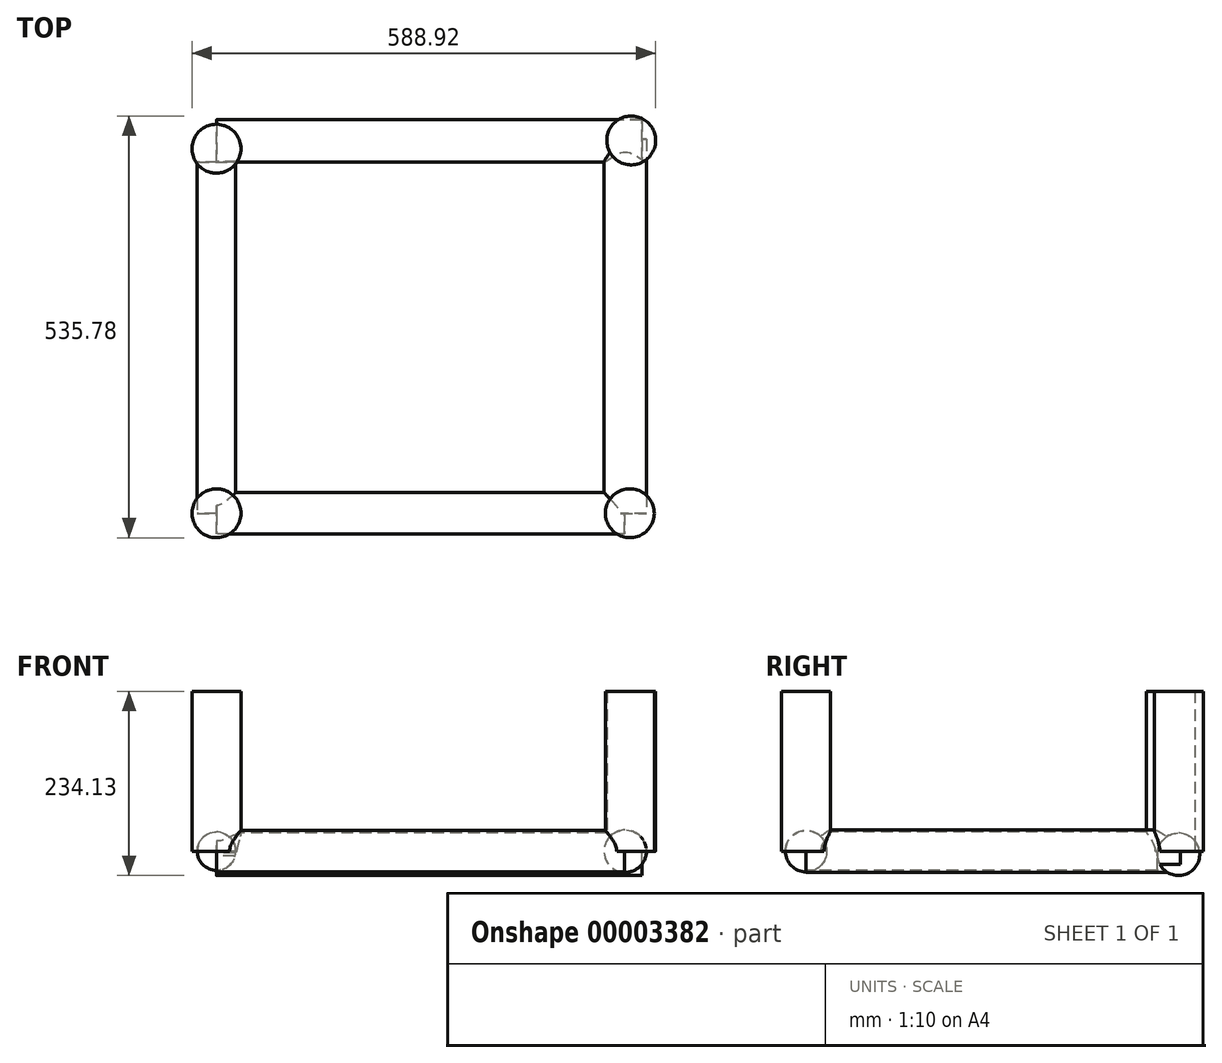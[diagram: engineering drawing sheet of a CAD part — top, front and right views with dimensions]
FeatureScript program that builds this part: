
annotation { "Feature Type Name" : "Feature", "Feature Type Description" : "" }
export const myFeature = defineFeature(function(context is Context, id is Id, definition is map)
    precondition{}
    {
        {
            var Q0;
            Q0=qCreatedBy(makeId("Front.planeOp"),FACE);
            var sketch = newSketch(context, id + "F0", { "sketchPlane" : qUnion([Q0])});
            skCircle(sketch, "E0", {"center": v(0, 0) * mm, "radius": 24.35 * mm});
            skSolve(sketch);
        }
        {
            var Q0;
            Q0=makeQuery(id+"F0.imprint","IMPRINT",FACE,{"disambiguationData":[TD([[makeQuery(id+"F0.imprint","IMPRINT",EDGE,{"derivedFrom":sQuery(id+"F0.wireOp",EDGE,"E0")}),1.0]])]});
            extrude(context, id + "F1", {"entities" : qUnion([Q0]), "oppositeDirection" : true, "depth" : 446.25 * mm});
        }
        {
            var Q0;
            Q0=qCreatedBy(makeId("Right.planeOp"),FACE);
            var sketch = newSketch(context, id + "F2", { "sketchPlane" : qUnion([Q0])});
            skCircle(sketch, "E1", {"center": v(0, 0) * mm, "radius": 26.23 * mm});
            skSolve(sketch);
        }
        {
            var Q0;
            Q0=makeQuery(id+"F2.imprint","IMPRINT",FACE,{"disambiguationData":[TD([[makeQuery(id+"F2.imprint","IMPRINT",EDGE,{"derivedFrom":sQuery(id+"F2.wireOp",EDGE,"E1")}),1.0]])]});
            extrude(context, id + "F3", {"entities" : qUnion([Q0]), "operationType" : NewBodyOperationType.ADD, "depth" : 518.32 * mm});
        }
        {
            var Q0;
            Q0=qCreatedBy(makeId("Front.planeOp"),FACE);
            var sketch = newSketch(context, id + "F4", { "sketchPlane" : qUnion([Q0])});
            skCircle(sketch, "E2", {"center": v(519.19, 0) * mm, "radius": 26.9 * mm});
            skSolve(sketch);
        }
        {
            var Q0;
            Q0=makeQuery(id+"F4.imprint","IMPRINT",FACE,{"disambiguationData":[TD([[makeQuery(id+"F4.imprint","IMPRINT",EDGE,{"derivedFrom":sQuery(id+"F4.wireOp",EDGE,"E2")}),1.0]])]});
            extrude(context, id + "F5", {"entities" : qUnion([Q0]), "operationType" : NewBodyOperationType.ADD, "oppositeDirection" : true, "depth" : 475.33 * mm});
        }
        {
            var Q0;
            Q0=qCreatedBy(makeId("Right.planeOp"),FACE);
            var sketch = newSketch(context, id + "F6", { "sketchPlane" : qUnion([Q0])});
            skCircle(sketch, "E3", {"center": v(473.13, -3.98) * mm, "radius": 26.95 * mm});
            skSolve(sketch);
        }
        {
            var Q0;
            Q0=makeQuery(id+"F6.imprint","IMPRINT",FACE,{"disambiguationData":[TD([[makeQuery(id+"F6.imprint","IMPRINT",EDGE,{"derivedFrom":sQuery(id+"F6.wireOp",EDGE,"E3")}),1.0]])]});
            extrude(context, id + "F7", {"entities" : qUnion([Q0]), "operationType" : NewBodyOperationType.ADD, "depth" : 540.38 * mm});
        }
        {
            var Q0;
            Q0=qCreatedBy(makeId("Top.planeOp"),FACE);
            var sketch = newSketch(context, id + "F8", { "sketchPlane" : qUnion([Q0])});
            skCircle(sketch, "E4", {"center": v(0, 0) * mm, "radius": 31.05 * mm});
            skCircle(sketch, "E5", {"center": v(0, 463.12) * mm, "radius": 31.05 * mm});
            skCircle(sketch, "E6", {"center": v(526.82, 473.68) * mm, "radius": 31.05 * mm});
            skCircle(sketch, "E7", {"center": v(525.12, 0) * mm, "radius": 31.05 * mm});
            skSolve(sketch);
        }
        {
            var Q0;
            {Q0=qUnion([makeQuery(id+"F8.imprint","IMPRINT",FACE,{"disambiguationData":[TD([[makeQuery(id+"F8.imprint","IMPRINT",EDGE,{"derivedFrom":sQuery(id+"F8.wireOp",EDGE,"E4")}),1.0]])]}),makeQuery(id+"F8.imprint","IMPRINT",FACE,{"disambiguationData":[TD([[makeQuery(id+"F8.imprint","IMPRINT",EDGE,{"derivedFrom":sQuery(id+"F8.wireOp",EDGE,"E5")}),1.0]])]}),makeQuery(id+"F8.imprint","IMPRINT",FACE,{"disambiguationData":[TD([[makeQuery(id+"F8.imprint","IMPRINT",EDGE,{"derivedFrom":sQuery(id+"F8.wireOp",EDGE,"E6")}),1.0]])]}),makeQuery(id+"F8.imprint","IMPRINT",FACE,{"disambiguationData":[TD([[makeQuery(id+"F8.imprint","IMPRINT",EDGE,{"derivedFrom":sQuery(id+"F8.wireOp",EDGE,"E7")}),1.0]])]})]);}
            extrude(context, id + "F9", {"entities" : qUnion([Q0]), "operationType" : NewBodyOperationType.ADD, "depth" : 203.2 * mm});
        }
    });
